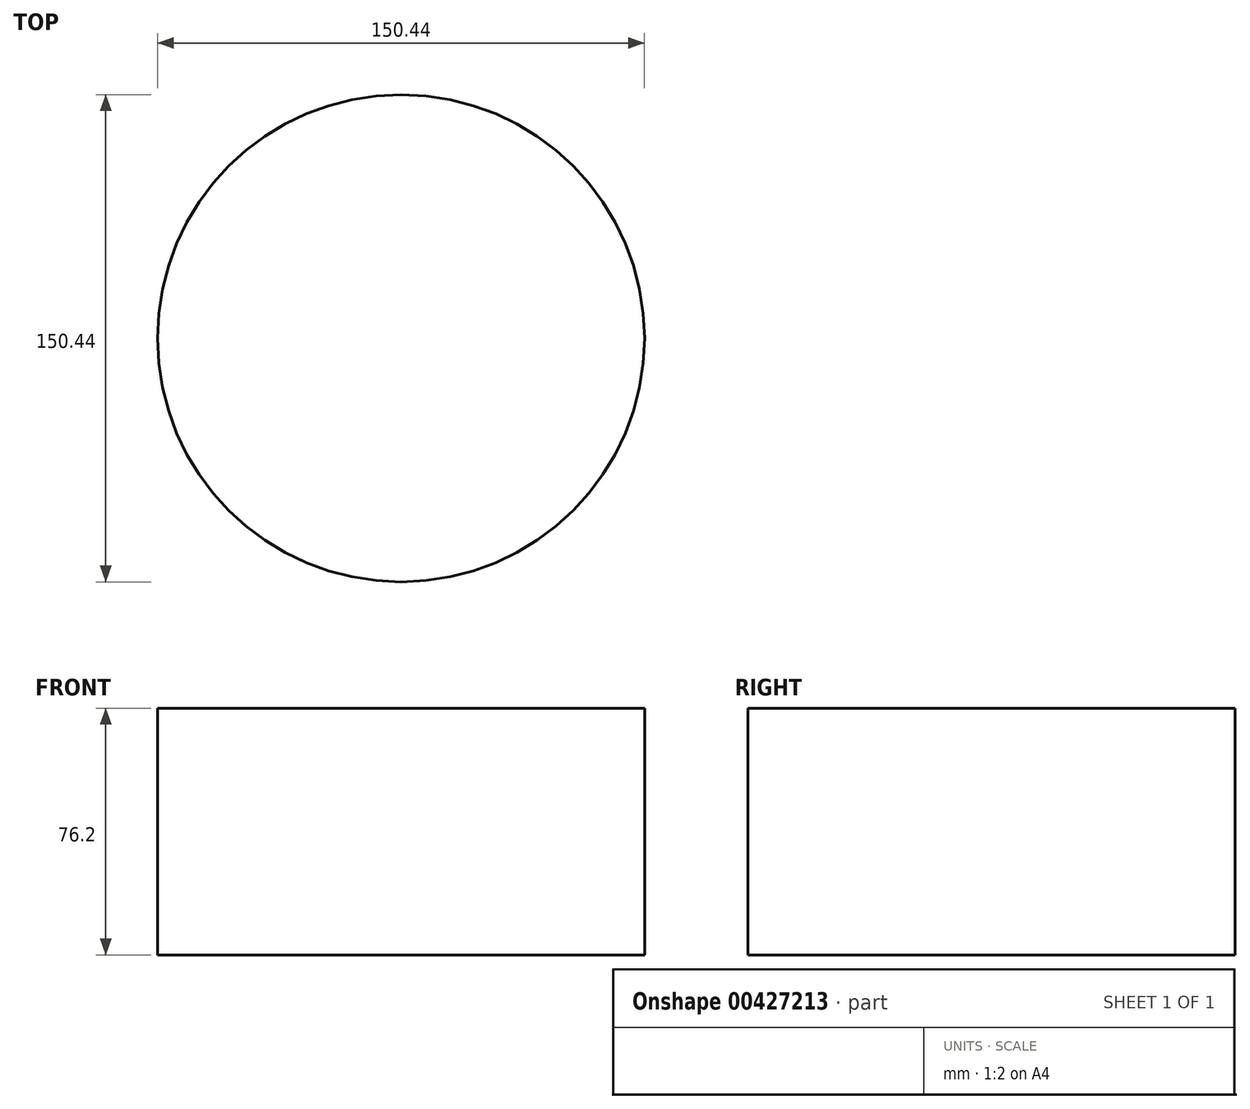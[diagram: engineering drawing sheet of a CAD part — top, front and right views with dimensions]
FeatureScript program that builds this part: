
annotation { "Feature Type Name" : "Feature", "Feature Type Description" : "" }
export const myFeature = defineFeature(function(context is Context, id is Id, definition is map)
    precondition{}
    {
        {
            var Q0;
            Q0=qCreatedBy(makeId("Top.planeOp"),FACE);
            var sketch = newSketch(context, id + "F0", { "sketchPlane" : qUnion([Q0])});
            skCircle(sketch, "E0", {"center": v(0, 0) * mm, "radius": 75.22 * mm});
            skSolve(sketch);
        }
        {
            var Q0;
            Q0=makeQuery(id+"F0.imprint","IMPRINT",FACE,{"disambiguationData":[TD([[makeQuery(id+"F0.imprint","IMPRINT",EDGE,{"derivedFrom":sQuery(id+"F0.wireOp",EDGE,"E0")}),1.0]])]});
            extrude(context, id + "F1", {"entities" : qUnion([Q0]), "depth" : 76.2 * mm});
        }
    });
